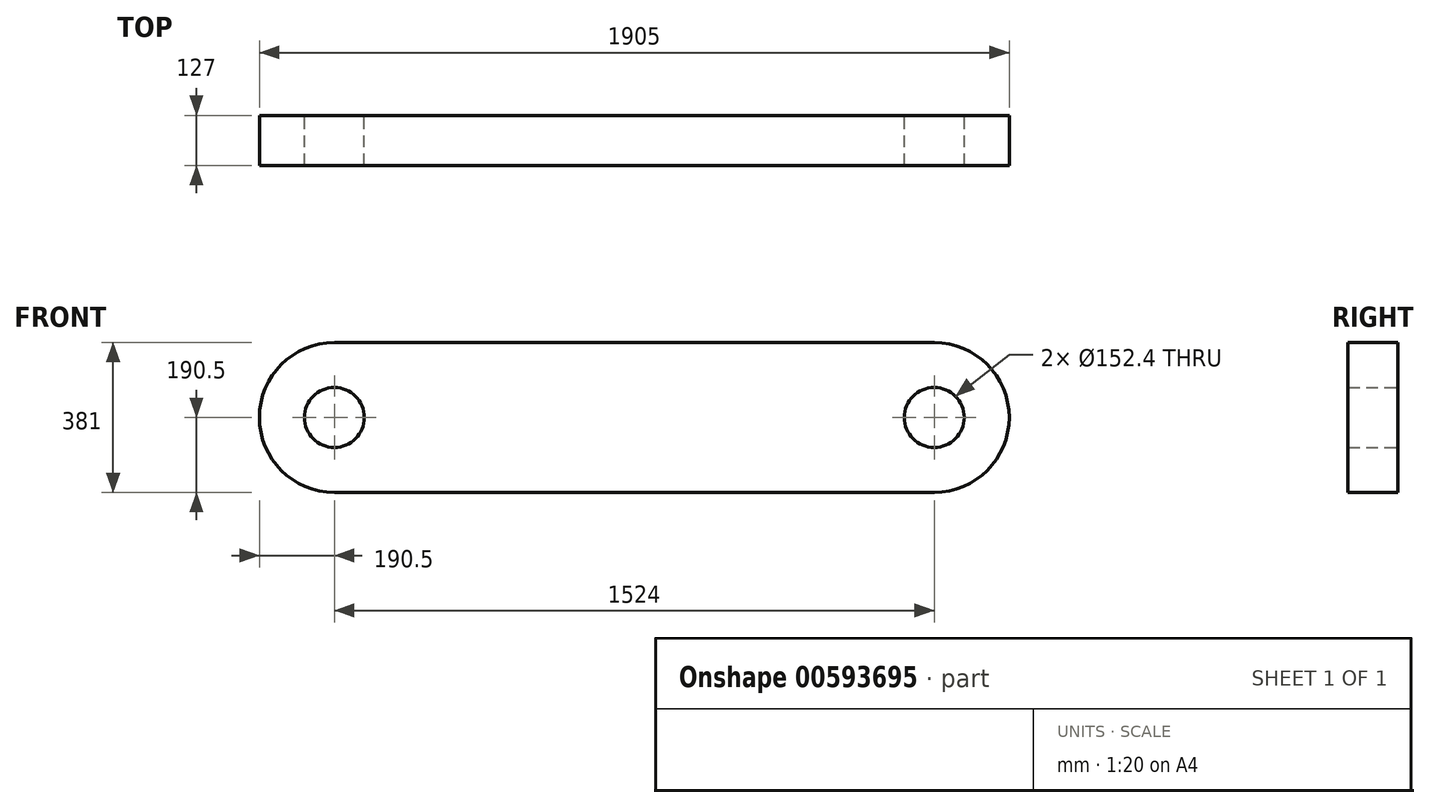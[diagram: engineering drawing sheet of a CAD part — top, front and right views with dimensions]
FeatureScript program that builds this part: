
annotation { "Feature Type Name" : "Feature", "Feature Type Description" : "" }
export const myFeature = defineFeature(function(context is Context, id is Id, definition is map)
    precondition{}
    {
        {
            var Q0;
            Q0=qCreatedBy(makeId("Front.planeOp"),FACE);
            var sketch = newSketch(context, id + "F0", { "sketchPlane" : qUnion([Q0])});
            skLineSegment(sketch, "E0.bottom", {"start": v(-762, 190.5) * mm, "end": v(762, 190.5) * mm});
            skLineSegment(sketch, "E0.top", {"start": v(-762, -190.5) * mm, "end": v(762, -190.5) * mm});
            skLineSegment(sketch, "E0.left", {"start": v(-762, 190.5) * mm, "end": v(-762, -190.5) * mm, "construction": true});
            skLineSegment(sketch, "E0.right", {"start": v(762, 190.5) * mm, "end": v(762, -190.5) * mm, "construction": true});
            skArc(sketch, "E1", {"start": v(-762, 190.5) * mm, "mid": v(-952.5, 0) * mm, "end": v(-762, -190.5) * mm});
            skArc(sketch, "E2.MirrorCS", {"start": v(762, 190.5) * mm, "mid": v(952.5, 0) * mm, "end": v(762, -190.5) * mm});
            skCircle(sketch, "E3", {"center": v(-762, 0) * mm, "radius": 76.2 * mm});
            skCircle(sketch, "E4", {"center": v(762, 0) * mm, "radius": 76.2 * mm});
            skSolve(sketch);
        }
        {
            var Q0;
            Q0 = qSketchRegion(id + "F0", true);
            extrude(context, id + "F1", {"entities" : qUnion([Q0]), "depth" : 127 * mm, "offsetDistance" : 25.4 * mm});
        }
    });
